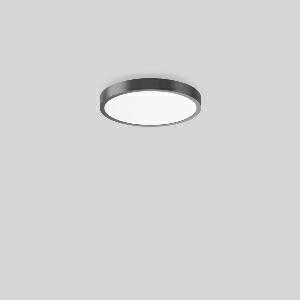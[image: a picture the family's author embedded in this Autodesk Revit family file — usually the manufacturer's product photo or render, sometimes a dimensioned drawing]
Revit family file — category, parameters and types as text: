
# Revit family: triona_round_a_312419_0031_730_8439
name_source: partatom
category: Lighting Fixtures
units: mm (PartAtom-declared; Revit-internal decimal feet)

## family parameters
Cut with Voids When Loaded = No
Host = Face
Light Source = No
Part Type = Normal
Room Calculation Point = No
Round Connector Dimension = Use Diameter
Shared = No

## types (1)
- TRIONA round A (1 x LED Modul 830, 4650 lm, 3000)
    Apparent Load = 48 VA
    CIE Flux Codes = 49 80 96 100 100
    Color Rendering = 80
    Color Temperature = 3000
    Default Elevation = 1800 mm
    Description = Series: TRIONA round
Decorative round LED surface-mounted luminaire. Flat, seamless frame: aluminium extrusion profile, powder coated. Cover made of sheet steel, powder-coated. Light emission through a diffuser: plastic, opal. Lightguide and diffuser made of non-yellowing plastic (PMMA). Lateral light emission (RZB SIDELITE technology) for above-average homogeneous light distribution. Suitable for Ceiling mounting, Wall (surface). Tool-free mounting via bayonet connection. Electronic ballast included. Very easy installation thanks to Plug+Play connection. With Casambi smart+free Bluetooth control for wireless network and operation using Android / iOS devices, free app available for download. 
Colour: anthracite metallic (DB703)
Diameter: 461 mm
Height: 88 mm
Lamp: LED
Socket: without socket
Colour temperature: 3000K
Colour rendering index (CRI): 80
System power: 48 W
Rated luminous flux: 4650 lm
Luminous efficiency: 97 lm/W
Control gear: Dimmable Bluetooth converter
Protection class: I
Type of protection: IP 20
    Height = 88 mm
    Lamp = 1 x LED Modul 830
    Lamp Light Flux = 4650 lm
    Lamp count = 1
    Length = 461 mm
    Lifetime = 50000 h
    Luminous efficacy = 97 lm/W
    Manufacturer = RZB
    ModVariant = No
    Model = 312419.0031.730
    Mounting Place = Ceiling
    Mounting Type = Surface mounted
    Number of Poles = 1
    OnlyDefault = Yes
    Power Factor = 1
    Product Name = TRIONA round A
    Product group = Surface mounted modular luminaires
    ProductGroupID = 306
    Protection Class = Protection class I
    Protection Degree = IP 20
    RLX_Detail_Level = 1
    RLX_Emergency_Light_Flux = 0 lm
    RLX_Emergency_Type = 0
    RLX_Emergency_Type_DB = No
    RlxData = <blob elided: 28741 chars, md5=23c4e4ec>
    Socket = socket
    Standby Power = 0 W
    System Light Flux = 4650 lm
    System Power = 48 W
    Type Comments = Product without accessories
    Type Image = 312420.0031.jpg
    URL = http://relux.com
    VarID = ---
    Voltage = 230 V
    Voltage Range = 220-240 V
    Weight = 0.00 kg
    Width = 0 mm  [stored 0 ft]

note: [stored X ft] marks values corroborated as IEEE doubles in the binary element streams (Revit-internal decimal feet)

## geometry (parser evidence)
native form markers: Blend x4, Sweep x10
no freeform markers — native parametric forms only
